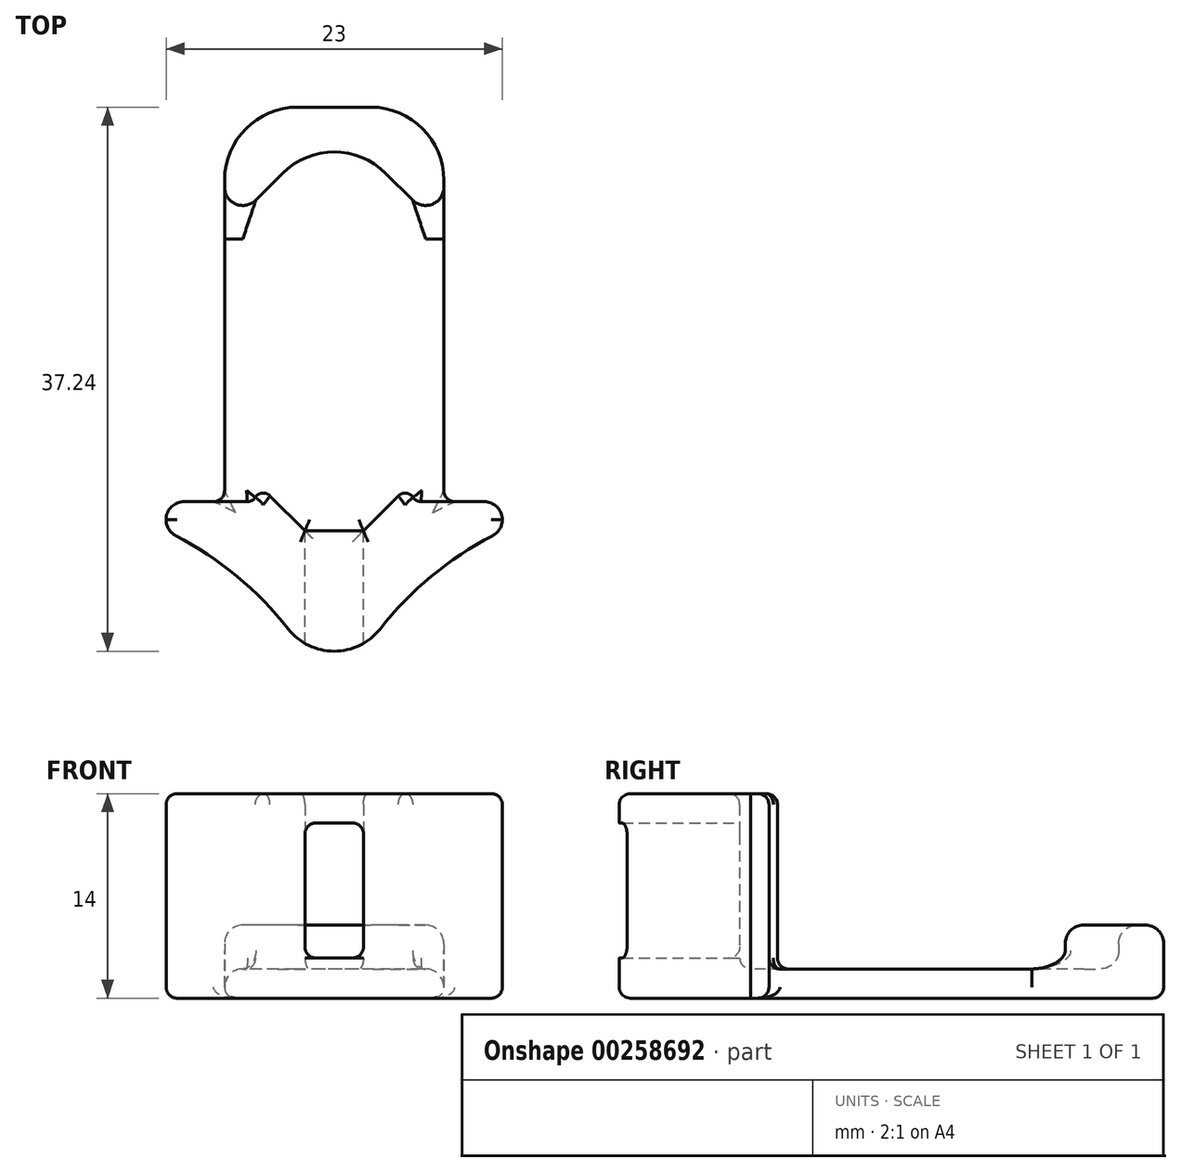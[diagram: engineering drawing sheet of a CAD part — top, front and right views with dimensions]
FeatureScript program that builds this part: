
annotation { "Feature Type Name" : "Feature", "Feature Type Description" : "" }
export const myFeature = defineFeature(function(context is Context, id is Id, definition is map)
    precondition{}
    {
        {
            var Q0;
            Q0=qCreatedBy(makeId("Top.planeOp"),FACE);
            var sketch = newSketch(context, id + "F0", { "sketchPlane" : qUnion([Q0])});
            skLineSegment(sketch, "E0", {"start": v(0, 0) * mm, "end": v(-10, 0) * mm});
            skLineSegment(sketch, "E1", {"start": v(-10, 0) * mm, "end": v(-5, 0) * mm});
            skLineSegment(sketch, "E2", {"start": v(-4, 2) * mm, "end": v(-10, 2) * mm});
            skLineSegment(sketch, "E3", {"start": v(-10, 2) * mm, "end": v(-10, 0) * mm});
            skLineSegment(sketch, "E4", {"start": v(0, 0) * mm, "end": v(1.5, 0) * mm});
            skLineSegment(sketch, "E5.MirrorCS", {"start": v(13, 0) * mm, "end": v(8, 0) * mm});
            skLineSegment(sketch, "E6.MirrorCS", {"start": v(3, 0) * mm, "end": v(1.5, 0) * mm});
            skLineSegment(sketch, "E7.MirrorCS", {"start": v(3, 0) * mm, "end": v(13, 0) * mm});
            skLineSegment(sketch, "E8.MirrorCS", {"start": v(7, 2) * mm, "end": v(13, 2) * mm});
            skLineSegment(sketch, "E9.MirrorCS", {"start": v(13, 2) * mm, "end": v(13, 0) * mm});
            skArc(sketch, "E10", {"start": v(1.5, -12) * mm, "mid": v(-3.17, -4.96) * mm, "end": v(-10, 0) * mm});
            skArc(sketch, "E11", {"start": v(13, 0) * mm, "mid": v(6.17, -4.96) * mm, "end": v(1.5, -12) * mm});
            skLineSegment(sketch, "E12", {"start": v(1.5, 0) * mm, "end": v(1.5, 27) * mm});
            skLineSegment(sketch, "E13", {"start": v(1.5, 27) * mm, "end": v(1.5, 19.5) * mm});
            skLineSegment(sketch, "E14", {"start": v(9, 19.5) * mm, "end": v(9, 2) * mm});
            skLineSegment(sketch, "E15", {"start": v(-6, 19.5) * mm, "end": v(-6, 2) * mm});
            skLineSegment(sketch, "E16", {"start": v(9, 19.5) * mm, "end": v(9, 27) * mm});
            skLineSegment(sketch, "E17", {"start": v(-6, 27) * mm, "end": v(-6, 19.5) * mm});
            skLineSegment(sketch, "E18", {"start": v(9, 27) * mm, "end": v(9, 28) * mm});
            skLineSegment(sketch, "E19", {"start": v(-6, 28) * mm, "end": v(-6, 27) * mm});
            skLineSegment(sketch, "E20", {"start": v(3, 0) * mm, "end": v(3.5, 0) * mm});
            skLineSegment(sketch, "E21", {"start": v(3.5, 0) * mm, "end": v(7, 3.5) * mm});
            skLineSegment(sketch, "E22", {"start": v(7, 3.5) * mm, "end": v(7, 2) * mm});
            skLineSegment(sketch, "E23", {"start": v(0, 0) * mm, "end": v(-0.5, 0) * mm});
            skLineSegment(sketch, "E24", {"start": v(-0.5, 0) * mm, "end": v(-4, 3.5) * mm});
            skLineSegment(sketch, "E25", {"start": v(-4, 3.5) * mm, "end": v(-4, 2) * mm});
            skLineSegment(sketch, "E26", {"start": v(9, 28) * mm, "end": v(9, 29) * mm});
            skLineSegment(sketch, "E27", {"start": v(-6, 28) * mm, "end": v(-6, 29) * mm});
            skLineSegment(sketch, "E28", {"start": v(-6, 29) * mm, "end": v(9, 29) * mm});
            skLineSegment(sketch, "E29", {"start": v(1.5, 27) * mm, "end": v(1.5, 28) * mm});
            skLineSegment(sketch, "E30", {"start": v(1.5, 28) * mm, "end": v(-6, 20.5) * mm});
            skLineSegment(sketch, "E31", {"start": v(1.5, 28) * mm, "end": v(9, 20.5) * mm});
            skSolve(sketch);
        }
        {
            var Q0;
            {var subQ2=sQuery(id+"F0.wireOp",EDGE,"E6.MirrorCS");Q0=makeQuery(id+"F0.imprint","IMPRINT",FACE,{"disambiguationData":[TD([[makeQuery(id+"F0.imprint","IMPRINT",EDGE,{"derivedFrom":subQ2}),-1.0]])]});}
            var Q1;
            {var subQ2=sQuery(id+"F0.wireOp",EDGE,"E4");Q1=makeQuery(id+"F0.imprint","IMPRINT",FACE,{"disambiguationData":[TD([[makeQuery(id+"F0.imprint","IMPRINT",EDGE,{"derivedFrom":subQ2}),1.0]])]});}
            var Q2;
            Q2=makeQuery(id+"F0.imprint","IMPRINT",FACE,{"disambiguationData":[TD([[makeQuery(id+"F0.imprint","IMPRINT",EDGE,{"derivedFrom":sQuery(id+"F0.wireOp",EDGE,"TIaFqpIp-Fas2-oKRo-Ii30-sfsPQyHIgsP7")}),1.0]])]});
            var Q3;
            Q3=makeQuery(id+"F0.imprint","IMPRINT",FACE,{"disambiguationData":[TD([[makeQuery(id+"F0.imprint","IMPRINT",EDGE,{"derivedFrom":sQuery(id+"F0.wireOp",EDGE,"57d91d50-4697-4c10-b57c-7c5841b1236b0.MirrorCS")}),1.0]])]});
            var Q4;
            {var subQ2=sQuery(id+"F0.wireOp",EDGE,"E4");Q4=makeQuery(id+"F0.imprint","IMPRINT",FACE,{"disambiguationData":[TD([[makeQuery(id+"F0.imprint","IMPRINT",EDGE,{"derivedFrom":subQ2}),-1.0]])]});}
            var Q5;
            {var subQ2=sQuery(id+"F0.wireOp",EDGE,"vKhJeFix-opGM-E1oq-6OqW-WgvPNorIo4HJ");Q5=makeQuery(id+"F0.imprint","IMPRINT",FACE,{"disambiguationData":[TD([[makeQuery(id+"F0.imprint","IMPRINT",EDGE,{"derivedFrom":subQ2}),1.0]])]});}
            var Q6;
            {var subQ3=sQuery(id+"F0.wireOp",EDGE,"E3");Q6=makeQuery(id+"F0.imprint","IMPRINT",FACE,{"disambiguationData":[TD([[makeQuery(id+"F0.imprint","IMPRINT",EDGE,{"derivedFrom":subQ3}),1.0]])]});}
            var Q7;
            {var subQ2=sQuery(id+"F0.wireOp",EDGE,"E4");Q7=makeQuery(id+"F0.imprint","IMPRINT",FACE,{"disambiguationData":[TD([[makeQuery(id+"F0.imprint","IMPRINT",EDGE,{"derivedFrom":subQ2}),-1.0]])]});}
            var Q8;
            {var subQ2=sQuery(id+"F0.wireOp",EDGE,"E4");Q8=makeQuery(id+"F0.imprint","IMPRINT",FACE,{"disambiguationData":[TD([[makeQuery(id+"F0.imprint","IMPRINT",EDGE,{"derivedFrom":subQ2}),-1.0]])]});}
            var Q9;
            {var subQ3=sQuery(id+"F0.wireOp",EDGE,"y7iBectg-4sOJ-2CRp-Imgd-6Q5hi3iqKadU");Q9=makeQuery(id+"F0.imprint","IMPRINT",FACE,{"disambiguationData":[TD([[makeQuery(id+"F0.imprint","IMPRINT",EDGE,{"derivedFrom":subQ3}),1.0]])]});}
            var Q10;
            {var subQ0=sQuery(id+"F0.wireOp",EDGE,"57d91d50-4697-4c10-b57c-7c5841b1236b2.MirrorCS");Q10=makeQuery(id+"F0.imprint","IMPRINT",FACE,{"disambiguationData":[TD([[makeQuery(id+"F0.imprint","IMPRINT",EDGE,{"derivedFrom":subQ0}),1.0]])]});}
            var Q11;
            Q11=makeQuery(id+"F0.imprint","IMPRINT",FACE,{"disambiguationData":[TD([[makeQuery(id+"F0.imprint","IMPRINT",EDGE,{"derivedFrom":sQuery(id+"F0.wireOp",EDGE,"57d91d50-4697-4c10-b57c-7c5841b1236b0.MirrorCS")}),-1.0]])]});
            var Q12;
            Q12=makeQuery(id+"F0.imprint","IMPRINT",FACE,{"disambiguationData":[TD([[makeQuery(id+"F0.imprint","IMPRINT",EDGE,{"derivedFrom":sQuery(id+"F0.wireOp",EDGE,"UFuvPjnE-Dxpt-Sqx3-x1IL-UVM6q10HGdxr")}),1.0]])]});
            var Q13;
            Q13=makeQuery(id+"F0.imprint","IMPRINT",FACE,{"disambiguationData":[TD([[makeQuery(id+"F0.imprint","IMPRINT",EDGE,{"derivedFrom":sQuery(id+"F0.wireOp",EDGE,"57d91d50-4697-4c10-b57c-7c5841b1236b2.MirrorCS")}),-1.0]])]});
            var Q14;
            {var subQ2=sQuery(id+"F0.wireOp",EDGE,"E6.MirrorCS");Q14=makeQuery(id+"F0.imprint","IMPRINT",FACE,{"disambiguationData":[TD([[makeQuery(id+"F0.imprint","IMPRINT",EDGE,{"derivedFrom":subQ2}),-1.0]])]});}
            var Q15;
            {var subQ2=sQuery(id+"F0.wireOp",EDGE,"E4");Q15=makeQuery(id+"F0.imprint","IMPRINT",FACE,{"disambiguationData":[TD([[makeQuery(id+"F0.imprint","IMPRINT",EDGE,{"derivedFrom":subQ2}),1.0]])]});}
            var Q16;
            {var subQ4=sQuery(id+"F0.wireOp",EDGE,"E5.MirrorCS");Q16=makeQuery(id+"F0.imprint","IMPRINT",FACE,{"disambiguationData":[TD([[makeQuery(id+"F0.imprint","IMPRINT",EDGE,{"derivedFrom":subQ4}),-1.0]])]});}
            extrude(context, id + "F1", {"entities" : qUnion([Q0, Q1, Q2, Q3, Q4, Q5, Q6, Q7, Q8, Q9, Q10, Q11, Q12, Q13, Q14, Q15, Q16]), "depth" : 2 * mm});
        }
        {
            var Q0;
            {var subQ4=sQuery(id+"F0.wireOp",EDGE,"E5.MirrorCS");Q0=makeQuery(id+"F0.imprint","IMPRINT",FACE,{"disambiguationData":[TD([[makeQuery(id+"F0.imprint","IMPRINT",EDGE,{"derivedFrom":subQ4}),-1.0]])]});}
            var Q1;
            {var subQ2=sQuery(id+"F0.wireOp",EDGE,"E4");Q1=makeQuery(id+"F0.imprint","IMPRINT",FACE,{"disambiguationData":[TD([[makeQuery(id+"F0.imprint","IMPRINT",EDGE,{"derivedFrom":subQ2}),-1.0]])]});}
            var Q2;
            {var subQ3=sQuery(id+"F0.wireOp",EDGE,"E3");Q2=makeQuery(id+"F0.imprint","IMPRINT",FACE,{"disambiguationData":[TD([[makeQuery(id+"F0.imprint","IMPRINT",EDGE,{"derivedFrom":subQ3}),1.0]])]});}
            extrude(context, id + "F2", {"entities" : qUnion([Q0, Q1, Q2]), "operationType" : NewBodyOperationType.ADD, "depth" : 14 * mm});
        }
        {
            var Q0;
            Q0=makeQuery(id+"F2.opExtrude","SWEPT_FACE",FACE,{"disambiguationData":[OSD([sQuery(id+"F0.wireOp",EDGE,"E0"),sQuery(id+"F0.wireOp",EDGE,"E4"),sQuery(id+"F0.wireOp",EDGE,"E6.MirrorCS"),sQuery(id+"F0.wireOp",EDGE,"E7.MirrorCS")])]});
            var sketch = newSketch(context, id + "F3", { "sketchPlane" : qUnion([Q0])});
            skLineSegment(sketch, "E32", {"start": v(-3.5, 2) * mm, "end": v(-3.5, 2.75) * mm});
            skLineSegment(sketch, "E33", {"start": v(-3.5, 2.75) * mm, "end": v(-3.5, 11.5) * mm});
            skLineSegment(sketch, "E34", {"start": v(0.5, 11.5) * mm, "end": v(0.5, 2.75) * mm});
            skLineSegment(sketch, "E35", {"start": v(0.5, 2.75) * mm, "end": v(-3.5, 2.75) * mm});
            skLineSegment(sketch, "E36", {"start": v(-3.5, 11.5) * mm, "end": v(-3.5, 12) * mm});
            skLineSegment(sketch, "E37", {"start": v(-3.5, 12) * mm, "end": v(0.5, 12) * mm});
            skLineSegment(sketch, "E38", {"start": v(0.5, 12) * mm, "end": v(0.5, 11.5) * mm});
            skSolve(sketch);
        }
        {
            var Q0;
            Q0=makeQuery(id+"F3.imprint","IMPRINT",FACE,{"disambiguationData":[TD([[makeQuery(id+"F3.imprint","IMPRINT",EDGE,{"derivedFrom":sQuery(id+"F3.wireOp",EDGE,"E33")}),1.0]])]});
            extrude(context, id + "F4", {"entities" : qUnion([Q0]), "operationType" : NewBodyOperationType.REMOVE, "oppositeDirection" : true, "depth" : 25 * mm});
        }
        {
            var Q0;
            {var subQ0=sQuery(id+"F0.wireOp",EDGE,"E10");var subQ1=sQuery(id+"F0.wireOp",EDGE,"E11");Q0=makeQuery(id+"F4.boolean.opBoolean","SPLIT",EDGE,{"disambiguationData":[TD([makeQuery(id+"F4.opExtrude","SWEPT_FACE",FACE,{"disambiguationData":[OSD([sQuery(id+"F3.wireOp",EDGE,"E35")])]})])],"derivedFrom":makeQuery(id+"F2.boolean.opBoolean","MERGE",EDGE,{"derivedFrom":[makeQuery(id+"F1.opExtrude","SWEPT_EDGE",EDGE,{"disambiguationData":[OSD([subQ0,subQ1])]}),makeQuery(id+"F2.opExtrude","SWEPT_EDGE",EDGE,{"disambiguationData":[OSD([subQ0,subQ1])]})]})});}
            var Q1;
            {var subQ0=sQuery(id+"F0.wireOp",EDGE,"E10");var subQ1=sQuery(id+"F0.wireOp",EDGE,"E11");Q1=makeQuery(id+"F4.boolean.opBoolean","SPLIT",EDGE,{"disambiguationData":[TD([makeQuery(id+"F4.opExtrude","SWEPT_FACE",FACE,{"disambiguationData":[OSD([sQuery(id+"F3.wireOp",EDGE,"M7ypVYgt-ZbFE-sRf5-vPSG-lUatdJ7ZvKMb")])]})])],"derivedFrom":makeQuery(id+"F2.boolean.opBoolean","MERGE",EDGE,{"derivedFrom":[makeQuery(id+"F1.opExtrude","SWEPT_EDGE",EDGE,{"disambiguationData":[OSD([subQ0,subQ1])]}),makeQuery(id+"F2.opExtrude","SWEPT_EDGE",EDGE,{"disambiguationData":[OSD([subQ0,subQ1])]})]})});}
            fillet(context, id + "F5", {"entities" : qUnion([Q0, Q1]), "radius" : 4 * mm, "tangentPropagation" : true, "allowEdgeOverflow" : false});
        }
        {
            var Q0;
            {var subQ0=sQuery(id+"F0.wireOp",EDGE,"E10");var subQ1=sQuery(id+"F0.wireOp",EDGE,"E3");var subQ2=sQuery(id+"F0.wireOp",EDGE,"E0");Q0=makeQuery(id+"F2.boolean.opBoolean","MERGE",EDGE,{"derivedFrom":[makeQuery(id+"F1.opExtrude","SWEPT_EDGE",EDGE,{"disambiguationData":[OSD([subQ2,subQ1,subQ0])]}),makeQuery(id+"F2.opExtrude","SWEPT_EDGE",EDGE,{"disambiguationData":[OSD([subQ2,subQ1,subQ0])]})]});}
            var Q1;
            {var subQ0=sQuery(id+"F0.wireOp",EDGE,"E3");var subQ1=sQuery(id+"F0.wireOp",EDGE,"E2");Q1=makeQuery(id+"F2.boolean.opBoolean","MERGE",EDGE,{"derivedFrom":[makeQuery(id+"F1.opExtrude","SWEPT_EDGE",EDGE,{"disambiguationData":[OSD([subQ1,subQ0])]}),makeQuery(id+"F2.opExtrude","SWEPT_EDGE",EDGE,{"disambiguationData":[OSD([subQ1,subQ0])]})]});}
            var Q2;
            {var subQ0=sQuery(id+"F0.wireOp",EDGE,"E11");var subQ1=sQuery(id+"F0.wireOp",EDGE,"E9.MirrorCS");var subQ2=sQuery(id+"F0.wireOp",EDGE,"E5.MirrorCS");Q2=makeQuery(id+"F2.boolean.opBoolean","MERGE",EDGE,{"derivedFrom":[makeQuery(id+"F1.opExtrude","SWEPT_EDGE",EDGE,{"disambiguationData":[OSD([subQ2,subQ1,subQ0])]}),makeQuery(id+"F2.opExtrude","SWEPT_EDGE",EDGE,{"disambiguationData":[OSD([subQ2,subQ1,subQ0])]})]});}
            var Q3;
            {var subQ0=sQuery(id+"F0.wireOp",EDGE,"E9.MirrorCS");var subQ1=sQuery(id+"F0.wireOp",EDGE,"E8.MirrorCS");Q3=makeQuery(id+"F2.boolean.opBoolean","MERGE",EDGE,{"derivedFrom":[makeQuery(id+"F1.opExtrude","SWEPT_EDGE",EDGE,{"disambiguationData":[OSD([subQ1,subQ0])]}),makeQuery(id+"F2.opExtrude","SWEPT_EDGE",EDGE,{"disambiguationData":[OSD([subQ1,subQ0])]})]});}
            var Q4;
            Q4=makeQuery(id+"FwZmR58LOXMJavg_0.opExtrude","SWEPT_EDGE",EDGE,{"disambiguationData":[OSD([sQuery(id+"F0.wireOp",EDGE,"ov0JZj1i-NSjB-XaGK-VkrS-mGTTpsvVBZmS"),sQuery(id+"F0.wireOp",EDGE,"UFuvPjnE-Dxpt-Sqx3-x1IL-UVM6q10HGdxr"),sQuery(id+"F0.wireOp",EDGE,"E15"),sQuery(id+"F0.wireOp",EDGE,"E17")])]});
            var Q5;
            Q5=makeQuery(id+"FwZmR58LOXMJavg_0.opExtrude","SWEPT_EDGE",EDGE,{"disambiguationData":[OSD([sQuery(id+"F0.wireOp",EDGE,"ejkm3t5n-kd5p-k1y4-sIzs-9kaZ14yq1ICi"),sQuery(id+"F0.wireOp",EDGE,"qQIeBH5h-3MJ0-f2hx-sWRG-OYla2PYHavGY"),sQuery(id+"F0.wireOp",EDGE,"E14"),sQuery(id+"F0.wireOp",EDGE,"E16")])]});
            var Q6;
            {var subQ0=sQuery(id+"F0.wireOp",EDGE,"E19");var subQ1=sQuery(id+"F0.wireOp",EDGE,"xrIySBCP-YeAG-MysN-XY5w-Bkx2l9SYpgEg");Q6=makeQuery(id+"FwZmR58LOXMJavg_0.boolean.opBoolean","MERGE",EDGE,{"derivedFrom":[makeQuery(id+"F1.opExtrude","SWEPT_EDGE",EDGE,{"disambiguationData":[OSD([subQ1,subQ0])]}),makeQuery(id+"FwZmR58LOXMJavg_0.opExtrude","SWEPT_EDGE",EDGE,{"disambiguationData":[OSD([subQ1,subQ0])]})]});}
            var Q7;
            {var subQ0=sQuery(id+"F0.wireOp",EDGE,"xrIySBCP-YeAG-MysN-XY5w-Bkx2l9SYpgEg");var subQ1=sQuery(id+"F0.wireOp",EDGE,"E18");Q7=makeQuery(id+"FwZmR58LOXMJavg_0.boolean.opBoolean","MERGE",EDGE,{"derivedFrom":[makeQuery(id+"F1.opExtrude","SWEPT_EDGE",EDGE,{"disambiguationData":[OSD([subQ1,subQ0])]}),makeQuery(id+"FwZmR58LOXMJavg_0.opExtrude","SWEPT_EDGE",EDGE,{"disambiguationData":[OSD([subQ1,subQ0])]})]});}
            fillet(context, id + "F6", {"entities" : qUnion([Q0, Q1, Q2, Q3, Q4, Q5, Q6, Q7]), "radius" : 1.25 * mm, "tangentPropagation" : true, "allowEdgeOverflow" : false});
        }
        {
            var Q0;
            Q0=makeQuery(id+"F2.opExtrude","SWEPT_EDGE",EDGE,{"disambiguationData":[OSD([sQuery(id+"F0.wireOp",EDGE,"E21"),sQuery(id+"F0.wireOp",EDGE,"E22")])]});
            var Q1;
            Q1=makeQuery(id+"F2.opExtrude","SWEPT_EDGE",EDGE,{"disambiguationData":[OSD([sQuery(id+"F0.wireOp",EDGE,"E24"),sQuery(id+"F0.wireOp",EDGE,"E25")])]});
            fillet(context, id + "F7", {"entities" : qUnion([Q0, Q1]), "radius" : .65 * mm, "tangentPropagation" : true, "allowEdgeOverflow" : false});
        }
        {
            var Q0;
            {var subQ0=sQuery(id+"F0.wireOp",EDGE,"E2");Q0=makeQuery(id+"F7.opFillet","BLEND_EDGE",EDGE,{"blendedFrom":[makeQuery(id+"F2.opExtrude","SWEPT_EDGE",EDGE,{"disambiguationData":[OSD([sQuery(id+"F0.wireOp",EDGE,"E24"),sQuery(id+"F0.wireOp",EDGE,"E25")])]}),makeQuery(id+"F2.boolean.opBoolean","MERGE",FACE,{"derivedFrom":[makeQuery(id+"F1.opExtrude","SWEPT_FACE",FACE,{"disambiguationData":[OSD([subQ0])]}),makeQuery(id+"F2.opExtrude","SWEPT_FACE",FACE,{"disambiguationData":[OSD([subQ0])]})]})],"blendedInto":[makeQuery(id+"F2.boolean.opBoolean","MERGE",FACE,{"derivedFrom":[makeQuery(id+"F1.opExtrude","SWEPT_FACE",FACE,{"disambiguationData":[OSD([subQ0])]}),makeQuery(id+"F2.opExtrude","SWEPT_FACE",FACE,{"disambiguationData":[OSD([subQ0])]})]})]});}
            var Q1;
            {var subQ0=sQuery(id+"F0.wireOp",EDGE,"E8.MirrorCS");Q1=makeQuery(id+"F7.opFillet","BLEND_EDGE",EDGE,{"blendedFrom":[makeQuery(id+"F2.opExtrude","SWEPT_EDGE",EDGE,{"disambiguationData":[OSD([sQuery(id+"F0.wireOp",EDGE,"E21"),sQuery(id+"F0.wireOp",EDGE,"E22")])]}),makeQuery(id+"F2.boolean.opBoolean","MERGE",FACE,{"derivedFrom":[makeQuery(id+"F1.opExtrude","SWEPT_FACE",FACE,{"disambiguationData":[OSD([subQ0])]}),makeQuery(id+"F2.opExtrude","SWEPT_FACE",FACE,{"disambiguationData":[OSD([subQ0])]})]})],"blendedInto":[makeQuery(id+"F2.boolean.opBoolean","MERGE",FACE,{"derivedFrom":[makeQuery(id+"F1.opExtrude","SWEPT_FACE",FACE,{"disambiguationData":[OSD([subQ0])]}),makeQuery(id+"F2.opExtrude","SWEPT_FACE",FACE,{"disambiguationData":[OSD([subQ0])]})]})]});}
            fillet(context, id + "F8", {"entities" : qUnion([Q0, Q1]), "radius" : .65 * mm, "tangentPropagation" : true, "allowEdgeOverflow" : false});
        }
        {
            var Q0;
            {var subQ0=sQuery(id+"F0.wireOp",EDGE,"E18");Q0=makeQuery(id+"F0.imprint","IMPRINT",FACE,{"disambiguationData":[TD([[makeQuery(id+"F0.imprint","IMPRINT",EDGE,{"derivedFrom":subQ0}),1.0]])]});}
            extrude(context, id + "F9", {"entities" : qUnion([Q0]), "operationType" : NewBodyOperationType.ADD, "depth" : 5 * mm});
        }
        {
            var Q0;
            Q0=makeQuery(id+"F9.opExtrude","SWEPT_EDGE",EDGE,{"disambiguationData":[OSD([sQuery(id+"F0.wireOp",EDGE,"E27"),sQuery(id+"F0.wireOp",EDGE,"E28")])]});
            var Q1;
            Q1=makeQuery(id+"F9.opExtrude","SWEPT_EDGE",EDGE,{"disambiguationData":[OSD([sQuery(id+"F0.wireOp",EDGE,"E26"),sQuery(id+"F0.wireOp",EDGE,"E28")])]});
            var Q2;
            Q2=makeQuery(id+"F9.opExtrude","SWEPT_EDGE",EDGE,{"disambiguationData":[OSD([sQuery(id+"F0.wireOp",EDGE,"E29"),sQuery(id+"F0.wireOp",EDGE,"E30"),sQuery(id+"F0.wireOp",EDGE,"E31")])]});
            fillet(context, id + "F10", {"entities" : qUnion([Q0, Q1, Q2]), "radius" : 5 * mm, "tangentPropagation" : true, "allowEdgeOverflow" : false});
        }
        {
            var Q0;
            Q0=makeQuery(id+"F9.opExtrude","SWEPT_EDGE",EDGE,{"disambiguationData":[OSD([sQuery(id+"F0.wireOp",EDGE,"E16"),sQuery(id+"F0.wireOp",EDGE,"E31")])]});
            var Q1;
            Q1=makeQuery(id+"F9.opExtrude","SWEPT_EDGE",EDGE,{"disambiguationData":[OSD([sQuery(id+"F0.wireOp",EDGE,"E17"),sQuery(id+"F0.wireOp",EDGE,"E30")])]});
            fillet(context, id + "F11", {"entities" : qUnion([Q0, Q1]), "radius" : 1.25 * mm, "tangentPropagation" : true, "allowEdgeOverflow" : false});
        }
        {
            var Q0;
            {var subQ0=sQuery(id+"F0.wireOp",EDGE,"E31");var subQ1=sQuery(id+"F0.wireOp",EDGE,"E30");Q0=makeQuery(id+"F10.opFillet","BLEND_EDGE",EDGE,{"blendedFrom":[makeQuery(id+"F9.opExtrude","SWEPT_EDGE",EDGE,{"disambiguationData":[OSD([sQuery(id+"F0.wireOp",EDGE,"E29"),subQ1,subQ0])]}),makeQuery(id+"F1.opExtrude","CAP_FACE",FACE,{"disambiguationData":[OSD([sQuery(id+"F0.wireOp",EDGE,"E2"),sQuery(id+"F0.wireOp",EDGE,"E3"),sQuery(id+"F0.wireOp",EDGE,"E8.MirrorCS"),sQuery(id+"F0.wireOp",EDGE,"E9.MirrorCS"),sQuery(id+"F0.wireOp",EDGE,"E10"),sQuery(id+"F0.wireOp",EDGE,"E11"),sQuery(id+"F0.wireOp",EDGE,"E14"),sQuery(id+"F0.wireOp",EDGE,"E15"),sQuery(id+"F0.wireOp",EDGE,"E16"),sQuery(id+"F0.wireOp",EDGE,"E17"),subQ1,subQ0])],"isStart":false})],"blendedInto":[makeQuery(id+"F1.opExtrude","CAP_FACE",FACE,{"disambiguationData":[OSD([sQuery(id+"F0.wireOp",EDGE,"E2"),sQuery(id+"F0.wireOp",EDGE,"E3"),sQuery(id+"F0.wireOp",EDGE,"E8.MirrorCS"),sQuery(id+"F0.wireOp",EDGE,"E9.MirrorCS"),sQuery(id+"F0.wireOp",EDGE,"E10"),sQuery(id+"F0.wireOp",EDGE,"E11"),sQuery(id+"F0.wireOp",EDGE,"E14"),sQuery(id+"F0.wireOp",EDGE,"E15"),sQuery(id+"F0.wireOp",EDGE,"E16"),sQuery(id+"F0.wireOp",EDGE,"E17"),subQ1,subQ0])],"isStart":false})]});}
            var Q1;
            Q1=makeQuery(id+"F1.opExtrude","CAP_EDGE",EDGE,{"disambiguationData":[OSD([sQuery(id+"F0.wireOp",EDGE,"E15"),sQuery(id+"F0.wireOp",EDGE,"E17")])],"isStart":false});
            var Q2;
            Q2=makeQuery(id+"F1.opExtrude","CAP_EDGE",EDGE,{"disambiguationData":[OSD([sQuery(id+"F0.wireOp",EDGE,"E14"),sQuery(id+"F0.wireOp",EDGE,"E16")])],"isStart":false});
            var Q3;
            {var subQ0=sQuery(id+"F0.wireOp",EDGE,"E31");var subQ1=sQuery(id+"F0.wireOp",EDGE,"E30");Q3=makeQuery(id+"F10.opFillet","BLEND_EDGE",EDGE,{"blendedFrom":[makeQuery(id+"F9.opExtrude","SWEPT_EDGE",EDGE,{"disambiguationData":[OSD([sQuery(id+"F0.wireOp",EDGE,"E29"),subQ1,subQ0])]}),makeQuery(id+"F9.opExtrude","CAP_FACE",FACE,{"disambiguationData":[OSD([sQuery(id+"F0.wireOp",EDGE,"E16"),sQuery(id+"F0.wireOp",EDGE,"E17"),sQuery(id+"F0.wireOp",EDGE,"E18"),sQuery(id+"F0.wireOp",EDGE,"E19"),sQuery(id+"F0.wireOp",EDGE,"E26"),sQuery(id+"F0.wireOp",EDGE,"E27"),sQuery(id+"F0.wireOp",EDGE,"E28"),subQ1,subQ0])],"isStart":false})],"blendedInto":[makeQuery(id+"F9.opExtrude","CAP_FACE",FACE,{"disambiguationData":[OSD([sQuery(id+"F0.wireOp",EDGE,"E16"),sQuery(id+"F0.wireOp",EDGE,"E17"),sQuery(id+"F0.wireOp",EDGE,"E18"),sQuery(id+"F0.wireOp",EDGE,"E19"),sQuery(id+"F0.wireOp",EDGE,"E26"),sQuery(id+"F0.wireOp",EDGE,"E27"),sQuery(id+"F0.wireOp",EDGE,"E28"),subQ1,subQ0])],"isStart":false})]});}
            fillet(context, id + "F12", {"entities" : qUnion([Q0, Q1, Q2, Q3]), "radius" : 1.25 * mm, "tangentPropagation" : true, "allowEdgeOverflow" : false});
        }
        {
            var Q0;
            {var subQ0=sQuery(id+"F0.wireOp",EDGE,"E31");var subQ1=sQuery(id+"F0.wireOp",EDGE,"E30");var subQ2=sQuery(id+"F0.wireOp",EDGE,"E17");var subQ3=sQuery(id+"F0.wireOp",EDGE,"E16");Q0=makeQuery(id+"F9.boolean.opBoolean","MERGE",FACE,{"derivedFrom":[makeQuery(id+"F1.opExtrude","CAP_FACE",FACE,{"disambiguationData":[OSD([sQuery(id+"F0.wireOp",EDGE,"E2"),sQuery(id+"F0.wireOp",EDGE,"E3"),sQuery(id+"F0.wireOp",EDGE,"E8.MirrorCS"),sQuery(id+"F0.wireOp",EDGE,"E9.MirrorCS"),sQuery(id+"F0.wireOp",EDGE,"E10"),sQuery(id+"F0.wireOp",EDGE,"E11"),sQuery(id+"F0.wireOp",EDGE,"E14"),sQuery(id+"F0.wireOp",EDGE,"E15"),subQ3,subQ2,subQ1,subQ0])],"isStart":true}),makeQuery(id+"F9.opExtrude","CAP_FACE",FACE,{"disambiguationData":[OSD([subQ3,subQ2,sQuery(id+"F0.wireOp",EDGE,"E18"),sQuery(id+"F0.wireOp",EDGE,"E19"),sQuery(id+"F0.wireOp",EDGE,"E26"),sQuery(id+"F0.wireOp",EDGE,"E27"),sQuery(id+"F0.wireOp",EDGE,"E28"),subQ1,subQ0])],"isStart":true})]});}
            var Q1;
            Q1=makeQuery(id+"F2.opExtrude","CAP_FACE",FACE,{"disambiguationData":[OSD([sQuery(id+"F0.wireOp",EDGE,"E0"),sQuery(id+"F0.wireOp",EDGE,"E2"),sQuery(id+"F0.wireOp",EDGE,"E3"),sQuery(id+"F0.wireOp",EDGE,"E4"),sQuery(id+"F0.wireOp",EDGE,"E6.MirrorCS"),sQuery(id+"F0.wireOp",EDGE,"E7.MirrorCS"),sQuery(id+"F0.wireOp",EDGE,"E8.MirrorCS"),sQuery(id+"F0.wireOp",EDGE,"E9.MirrorCS"),sQuery(id+"F0.wireOp",EDGE,"E10"),sQuery(id+"F0.wireOp",EDGE,"E11"),sQuery(id+"F0.wireOp",EDGE,"E21"),sQuery(id+"F0.wireOp",EDGE,"E22"),sQuery(id+"F0.wireOp",EDGE,"E24"),sQuery(id+"F0.wireOp",EDGE,"E25")])],"isStart":false});
            fillet(context, id + "F13", {"entities" : qUnion([Q0, Q1]), "radius" : .75 * mm, "tangentPropagation" : true, "allowEdgeOverflow" : false});
        }
        {
            var Q0;
            Q0=makeQuery(id+"F2.boolean.opBoolean","INTERSECT",EDGE,{"derivedFrom":[makeQuery(id+"F1.opExtrude","CAP_FACE",FACE,{"disambiguationData":[OSD([sQuery(id+"F0.wireOp",EDGE,"E2"),sQuery(id+"F0.wireOp",EDGE,"E3"),sQuery(id+"F0.wireOp",EDGE,"E8.MirrorCS"),sQuery(id+"F0.wireOp",EDGE,"E9.MirrorCS"),sQuery(id+"F0.wireOp",EDGE,"E10"),sQuery(id+"F0.wireOp",EDGE,"E11"),sQuery(id+"F0.wireOp",EDGE,"E14"),sQuery(id+"F0.wireOp",EDGE,"E15"),sQuery(id+"F0.wireOp",EDGE,"E16"),sQuery(id+"F0.wireOp",EDGE,"E17"),sQuery(id+"F0.wireOp",EDGE,"E30"),sQuery(id+"F0.wireOp",EDGE,"E31")])],"isStart":false}),makeQuery(id+"F2.opExtrude","SWEPT_FACE",FACE,{"disambiguationData":[OSD([sQuery(id+"F0.wireOp",EDGE,"E0"),sQuery(id+"F0.wireOp",EDGE,"E4"),sQuery(id+"F0.wireOp",EDGE,"E6.MirrorCS"),sQuery(id+"F0.wireOp",EDGE,"E7.MirrorCS")])]})]});
            var Q1;
            Q1=makeQuery(id+"F2.boolean.opBoolean","INTERSECT",EDGE,{"derivedFrom":[makeQuery(id+"F1.opExtrude","CAP_FACE",FACE,{"disambiguationData":[OSD([sQuery(id+"F0.wireOp",EDGE,"E2"),sQuery(id+"F0.wireOp",EDGE,"E3"),sQuery(id+"F0.wireOp",EDGE,"E8.MirrorCS"),sQuery(id+"F0.wireOp",EDGE,"E9.MirrorCS"),sQuery(id+"F0.wireOp",EDGE,"E10"),sQuery(id+"F0.wireOp",EDGE,"E11"),sQuery(id+"F0.wireOp",EDGE,"E14"),sQuery(id+"F0.wireOp",EDGE,"E15"),sQuery(id+"F0.wireOp",EDGE,"E16"),sQuery(id+"F0.wireOp",EDGE,"E17"),sQuery(id+"F0.wireOp",EDGE,"E30"),sQuery(id+"F0.wireOp",EDGE,"E31")])],"isStart":false}),makeQuery(id+"F2.opExtrude","SWEPT_FACE",FACE,{"disambiguationData":[OSD([sQuery(id+"F0.wireOp",EDGE,"E24")])]})]});
            var Q2;
            Q2=makeQuery(id+"F2.boolean.opBoolean","INTERSECT",EDGE,{"derivedFrom":[makeQuery(id+"F1.opExtrude","CAP_FACE",FACE,{"disambiguationData":[OSD([sQuery(id+"F0.wireOp",EDGE,"E2"),sQuery(id+"F0.wireOp",EDGE,"E3"),sQuery(id+"F0.wireOp",EDGE,"E8.MirrorCS"),sQuery(id+"F0.wireOp",EDGE,"E9.MirrorCS"),sQuery(id+"F0.wireOp",EDGE,"E10"),sQuery(id+"F0.wireOp",EDGE,"E11"),sQuery(id+"F0.wireOp",EDGE,"E14"),sQuery(id+"F0.wireOp",EDGE,"E15"),sQuery(id+"F0.wireOp",EDGE,"E16"),sQuery(id+"F0.wireOp",EDGE,"E17"),sQuery(id+"F0.wireOp",EDGE,"E30"),sQuery(id+"F0.wireOp",EDGE,"E31")])],"isStart":false}),makeQuery(id+"F2.opExtrude","SWEPT_FACE",FACE,{"disambiguationData":[OSD([sQuery(id+"F0.wireOp",EDGE,"E21")])]})]});
            fillet(context, id + "F14", {"entities" : qUnion([Q0, Q1, Q2]), "radius" : .75 * mm, "tangentPropagation" : true, "allowEdgeOverflow" : false});
        }
        {
            var Q0;
            Q0=makeQuery(id+"F4.boolean.opBoolean","COPY",EDGE,{"derivedFrom":makeQuery(id+"F4.opExtrude","SWEPT_EDGE",EDGE,{"disambiguationData":[OSD([sQuery(id+"F3.wireOp",EDGE,"E32"),sQuery(id+"F3.wireOp",EDGE,"E33"),sQuery(id+"F3.wireOp",EDGE,"E35")])]})});
            var Q1;
            Q1=makeQuery(id+"F4.boolean.opBoolean","COPY",EDGE,{"derivedFrom":makeQuery(id+"F4.opExtrude","SWEPT_EDGE",EDGE,{"disambiguationData":[OSD([sQuery(id+"F0.wireOp",EDGE,"E0"),sQuery(id+"F0.wireOp",EDGE,"E24"),sQuery(id+"F3.wireOp",EDGE,"E34"),sQuery(id+"F3.wireOp",EDGE,"E35")])]})});
            var Q2;
            Q2=makeQuery(id+"F4.boolean.opBoolean","COPY",EDGE,{"derivedFrom":makeQuery(id+"F4.opExtrude","SWEPT_EDGE",EDGE,{"disambiguationData":[OSD([sQuery(id+"F0.wireOp",EDGE,"E0"),sQuery(id+"F0.wireOp",EDGE,"E24"),sQuery(id+"F3.wireOp",EDGE,"E37"),sQuery(id+"F3.wireOp",EDGE,"E38")])]})});
            var Q3;
            Q3=makeQuery(id+"F4.boolean.opBoolean","COPY",EDGE,{"derivedFrom":makeQuery(id+"F4.opExtrude","SWEPT_EDGE",EDGE,{"disambiguationData":[OSD([sQuery(id+"F0.wireOp",EDGE,"E7.MirrorCS"),sQuery(id+"F0.wireOp",EDGE,"E21"),sQuery(id+"F3.wireOp",EDGE,"E36"),sQuery(id+"F3.wireOp",EDGE,"E37")])]})});
            fillet(context, id + "F15", {"entities" : qUnion([Q0, Q1, Q2, Q3]), "radius" : .75 * mm, "tangentPropagation" : true, "allowEdgeOverflow" : false});
        }
    });
